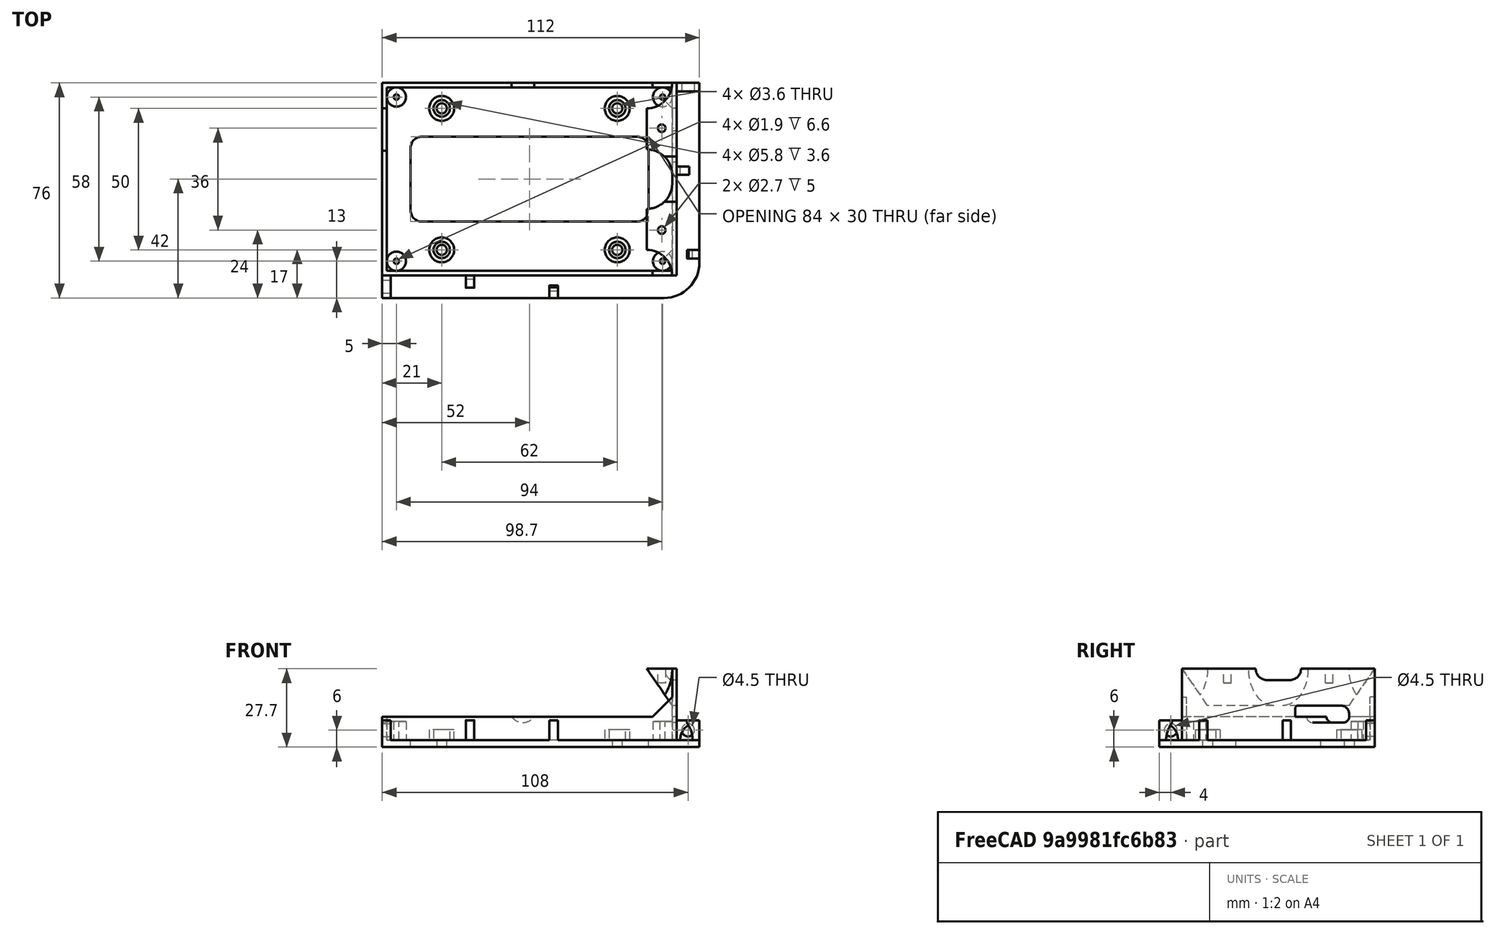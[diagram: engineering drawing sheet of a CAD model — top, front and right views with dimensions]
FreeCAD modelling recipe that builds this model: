
FCSTD DOCUMENT  (FreeCAD 1.0R39319 (Git))
Label: NanoPC-Rail
License: All rights reserved
LicenseURL: https://en.wikipedia.org/wiki/All_rights_reserved
objects: Sketcher::SketchObject×22, PartDesign::Pocket×13, PartDesign::Pad×9, App::VarSet×1, PartDesign::Body×1
note: 111 computed .brp shape members not serialized (recipe doc carries the construction recipe); baked Part::Feature solids carry a one-line shape summary decoded from their .brp

FEATURE [App::VarSet] VarSet
  BlackSelfTappingDiameter = 2.7
  Border = 8.2
  DX = 104
  DY = 68
  HoleDX = 94
  HoleDY = 58
  M3HeadDiameter = 5.8
  M3PassThroughDiameter = 3.6
  MiniBlackSelfTappingDiameter = 1.9
  PcbDX = 100.8
  PcbDY = 64.8
  PoleDiameter = 6.8
  PoleHeight = 6.6
  RailScrewDistance = 62
  Thickness = 2.5
  TopPcbWallHeight = 17
  WallThickness = 1.6
  expr: DX = PcbDX + 2 * WallThickness
  expr: DY = PcbDY + 2 * WallThickness
FEATURE [Sketcher::SketchObject] Sketch
  ArcFitTolerance = 1e-06
  AttachmentSupport = -> [XY_Plane]
  FullyConstrained = true
  MakeInternals = false
  MapMode = 5
  expr: Constraints[10] = VarSet.DY
  expr: Constraints[56] = VarSet.RailScrewDistance
  expr: Constraints[62] = VarSet.M3PassThroughDiameter
  expr: Constraints[9] = VarSet.DX
  sketch-geometry (29):
    g0: LineSegment StartX=-52 StartY=34 StartZ=0 EndX=-52 EndY=-34 EndZ=0
    g1: LineSegment [constr] StartX=-52 StartY=-34 StartZ=0 EndX=52 EndY=-34 EndZ=0
    g2: LineSegment [constr] StartX=52 StartY=-34 StartZ=0 EndX=52 EndY=34 EndZ=0
    g3: LineSegment StartX=52 StartY=34 StartZ=0 EndX=-52 EndY=34 EndZ=0
    g4: LineSegment StartX=-52 StartY=-34 StartZ=0 EndX=-52 EndY=-42 EndZ=0
    g5: LineSegment StartX=-52 StartY=-42 StartZ=0 EndX=47.5 EndY=-42 EndZ=0
    g6: LineSegment StartX=52 StartY=34 StartZ=0 EndX=60 EndY=34 EndZ=0
    g7: LineSegment StartX=60 StartY=34 StartZ=0 EndX=60 EndY=-29.5 EndZ=0
    g8: LineSegment StartX=-42 StartY=11 StartZ=0 EndX=-42 EndY=-11 EndZ=0
    g9: LineSegment StartX=-38 StartY=-15 StartZ=0 EndX=38 EndY=-15 EndZ=0
    g10: LineSegment StartX=42 StartY=-11 StartZ=0 EndX=42 EndY=11 EndZ=0
    g11: LineSegment StartX=38 StartY=15 StartZ=0 EndX=-38 EndY=15 EndZ=0
    g12: ArcOfCircle CenterX=-38 CenterY=11 CenterZ=0 NormalX=0 NormalY=0 NormalZ=1 AngleXU=0 Radius=4 StartAngle=1.5708 EndAngle=3.14159
    g13: ArcOfCircle CenterX=-38 CenterY=-11 CenterZ=0 NormalX=0 NormalY=0 NormalZ=1 AngleXU=0 Radius=4 StartAngle=3.14159 EndAngle=4.71239
    g14: ArcOfCircle CenterX=38 CenterY=-11 CenterZ=0 NormalX=0 NormalY=0 NormalZ=1 AngleXU=0 Radius=4 StartAngle=4.71239 EndAngle=6.28319
    g15: ArcOfCircle CenterX=38 CenterY=11 CenterZ=0 NormalX=0 NormalY=0 NormalZ=1 AngleXU=0 Radius=4 StartAngle=0 EndAngle=1.5708
    g16: GeomPoint [constr] X=-42 Y=15 Z=0
    g17: GeomPoint [constr] X=42 Y=-15 Z=0
    g18: LineSegment [constr] StartX=-42 StartY=11 StartZ=0 EndX=-52 EndY=11 EndZ=0
    g19: LineSegment [constr] StartX=-38 StartY=15 StartZ=0 EndX=-38 EndY=34 EndZ=0
    g20: ArcOfCircle CenterX=47.5 CenterY=-29.5 CenterZ=0 NormalX=0 NormalY=0 NormalZ=1 AngleXU=0 Radius=12.5 StartAngle=4.71239 EndAngle=6.28319
    g21: Circle CenterX=-31 CenterY=25 CenterZ=0 NormalX=0 NormalY=0 NormalZ=1 AngleXU=0 Radius=1.8
    g22: Circle CenterX=31 CenterY=25 CenterZ=0 NormalX=0 NormalY=0 NormalZ=1 AngleXU=0 Radius=1.8
    g23: LineSegment [constr] StartX=-31 StartY=25 StartZ=0 EndX=31 EndY=25 EndZ=0
    g24: LineSegment [constr] StartX=-31 StartY=25 StartZ=0 EndX=-31 EndY=34 EndZ=0
    g25: Circle CenterX=-31 CenterY=-25 CenterZ=0 NormalX=0 NormalY=0 NormalZ=1 AngleXU=0 Radius=1.8
    g26: Circle CenterX=31 CenterY=-25 CenterZ=0 NormalX=0 NormalY=0 NormalZ=1 AngleXU=0 Radius=1.8
    g27: LineSegment [constr] StartX=-31 StartY=-25 StartZ=0 EndX=31 EndY=-25 EndZ=0
    g28: LineSegment [constr] StartX=-31 StartY=-25 StartZ=0 EndX=-31 EndY=-34 EndZ=0
  constraints (73):
    c: Coincident(g0,g1)
    c: Coincident(g1,g2)
    c: Coincident(g2,g3)
    c: Coincident(g3,g0)
    c: Vertical(g0)
    c: Vertical(g2)
    c: Horizontal(g1)
    c: Horizontal(g3)
    c: Symmetric(g1,g0,g-1)
    c: Distance(g3) = 104
    c: Distance(g2) = 68
    c: Coincident(g4,g0)
    c: Vertical(g4)
    c: Coincident(g5,g4)
    c: Horizontal(g5)
    c: Coincident(g6,g2)
    c: Horizontal(g6)
    c: Coincident(g7,g6)
    c: Vertical(g7)
    c: Equal(g6,g4)
    c: Distance(g4) = 8
    c: Tangent(g8,g12) = -1.5708
    c: Tangent(g8,g13) = -1.5708
    c: Tangent(g9,g13) = -1.5708
    c: Tangent(g9,g14) = -1.5708
    c: Tangent(g10,g14) = -1.5708
    c: Tangent(g10,g15) = -1.5708
    c: Tangent(g11,g15) = -1.5708
    c: Tangent(g11,g12) = -1.5708
    c: Vertical(g8)
    c: Vertical(g10)
    c: Horizontal(g9)
    c: Horizontal(g11)
    c: Equal(g12,g13)
    c: Equal(g13,g14)
    c: Equal(g14,g15)
    c: PointOnObject(g16,g8)
    c: PointOnObject(g16,g11)
    c: PointOnObject(g17,g9)
    c: PointOnObject(g17,g10)
    c: Diameter(g15) = 8
    c: Symmetric(g16,g17,g-1)
    c: Coincident(g18,g8)
    c: PointOnObject(g18,g0)
    c: Horizontal(g18)
    c: Distance(g18) = 10
    c: Coincident(g19,g11)
    c: PointOnObject(g19,g3)
    c: Vertical(g19)
    c: Distance(g19) = 19
    c: Diameter(g20) = 25
    c: Tangent(g7,g20) = 1.5708
    c: Tangent(g5,g20) = -1.5708
    c: Symmetric(g21,g22,g-2)
    c: Coincident(g23,g21)
    c: Coincident(g23,g22)
    c: Distance(g23) = 62
    c: Coincident(g24,g21)
    c: PointOnObject(g24,g3)
    c: Vertical(g24)
    c: Distance(g24) = 9
    c: Equal(g22,g21)
    c: Diameter(g22) = 3.6
    c: Symmetric(g25,g26,g-2)
    c: Coincident(g27,g25)
    c: Coincident(g27,g26)
    c: Equal(g27,g23)
    c: Coincident(g28,g25)
    c: PointOnObject(g28,g1)
    c: Vertical(g28)
    c: Equal(g28,g24)
    c: Equal(g22,g26)
    c: Equal(g26,g25)
FEATURE [PartDesign::Pad] Pad  label="Base Structure"
  Direction = (0,0,1)
  Length = 2.5
  Length2 = 10
  Profile = -> Sketch
  ReferenceAxis = -> Sketch [N_Axis]
  Refine = true
  Suppressed = false
  Type = 0
  expr: Length = VarSet.Thickness
FEATURE [Sketcher::SketchObject] Sketch002
  ArcFitTolerance = 1e-06
  FullyConstrained = true
  MakeInternals = false
  MapMode = 5
  Placement = pos=(0,0,2.5) rot=(0,0,1;0rad)
  expr: Constraints[10] = VarSet.PcbDX
  expr: Constraints[17] = VarSet.DX
  expr: Constraints[20] = VarSet.DY
  expr: Constraints[9] = VarSet.PcbDY
  sketch-geometry (8):
    g0: LineSegment StartX=-50.4 StartY=32.4 StartZ=0 EndX=-50.4 EndY=-32.4 EndZ=0
    g1: LineSegment StartX=-50.4 StartY=-32.4 StartZ=0 EndX=50.4 EndY=-32.4 EndZ=0
    g2: LineSegment StartX=50.4 StartY=-32.4 StartZ=0 EndX=50.4 EndY=32.4 EndZ=0
    g3: LineSegment StartX=50.4 StartY=32.4 StartZ=0 EndX=-50.4 EndY=32.4 EndZ=0
    g4: LineSegment StartX=-52 StartY=34 StartZ=0 EndX=-52 EndY=-34 EndZ=0
    g5: LineSegment StartX=-52 StartY=-34 StartZ=0 EndX=52 EndY=-34 EndZ=0
    g6: LineSegment StartX=52 StartY=-34 StartZ=0 EndX=52 EndY=34 EndZ=0
    g7: LineSegment StartX=52 StartY=34 StartZ=0 EndX=-52 EndY=34 EndZ=0
  constraints (21):
    c: Coincident(g0,g1)
    c: Coincident(g1,g2)
    c: Coincident(g2,g3)
    c: Coincident(g3,g0)
    c: Vertical(g0)
    c: Vertical(g2)
    c: Horizontal(g1)
    c: Horizontal(g3)
    c: Symmetric(g1,g0,g-1)
    c: Distance(g2) = 64.8
    c: Distance(g3) = 100.8
    c: Coincident(g4,g5)
    c: Coincident(g5,g6)
    c: Coincident(g6,g7)
    c: Coincident(g7,g4)
    c: Horizontal(g5)
    c: Symmetric(g6,g4,g-2)
    c: Distance(g7) = 104
    c: Equal(g5,g7)
    c: Symmetric(g5,g6,g-1)
    c: Distance(g6) = 68
FEATURE [PartDesign::Pad] Pad001  label="Border"
  BaseFeature = -> Pad
  Direction = (0,0,1)
  Length = 8.2
  Length2 = 10
  Profile = -> Sketch002
  ReferenceAxis = -> Sketch002 [N_Axis]
  Refine = true
  Suppressed = false
  Type = 0
  expr: Length = VarSet.Border
FEATURE [Sketcher::SketchObject] Sketch003
  ArcFitTolerance = 1e-06
  AttachmentSupport = -> [Pad001]
  FullyConstrained = true
  MakeInternals = false
  MapMode = 5
  Placement = pos=(0,0,2.5) rot=(0,0,1;0rad)
  expr: Constraints[12] = VarSet.PoleDiameter
  expr: Constraints[20] = VarSet.MiniBlackSelfTappingDiameter
  expr: Constraints[5] = VarSet.HoleDX
  expr: Constraints[6] = VarSet.HoleDY
  sketch-geometry (10):
    g0: Circle CenterX=-47 CenterY=29 CenterZ=0 NormalX=0 NormalY=0 NormalZ=1 AngleXU=0 Radius=3.4
    g1: Circle CenterX=47 CenterY=29 CenterZ=0 NormalX=0 NormalY=0 NormalZ=1 AngleXU=0 Radius=3.4
    g2: Circle CenterX=47 CenterY=-29 CenterZ=0 NormalX=0 NormalY=0 NormalZ=1 AngleXU=0 Radius=3.4
    g3: Circle CenterX=-47 CenterY=-29 CenterZ=0 NormalX=0 NormalY=0 NormalZ=1 AngleXU=0 Radius=3.4
    g4: LineSegment [constr] StartX=-47 StartY=29 StartZ=0 EndX=47 EndY=29 EndZ=0
    g5: LineSegment [constr] StartX=47 StartY=29 StartZ=0 EndX=47 EndY=-29 EndZ=0
    g6: Circle CenterX=-47 CenterY=29 CenterZ=0 NormalX=0 NormalY=0 NormalZ=1 AngleXU=0 Radius=0.95
    g7: Circle CenterX=47 CenterY=29 CenterZ=0 NormalX=0 NormalY=0 NormalZ=1 AngleXU=0 Radius=0.95
    g8: Circle CenterX=47 CenterY=-29 CenterZ=0 NormalX=0 NormalY=0 NormalZ=1 AngleXU=0 Radius=0.95
    g9: Circle CenterX=-47 CenterY=-29 CenterZ=0 NormalX=0 NormalY=0 NormalZ=1 AngleXU=0 Radius=0.95
  constraints (21):
    c: Coincident(g4,g0)
    c: Coincident(g5,g1)
    c: Coincident(g5,g2)
    c: Coincident(g4,g1)
    c: Symmetric(g1,g0,g-2)
    c: Distance(g4) = 94
    c: Distance(g5) = 58
    c: Symmetric(g2,g1,g-1)
    c: Symmetric(g3,g2,g-2)
    c: Equal(g1,g2)
    c: Equal(g2,g3)
    c: Equal(g3,g0)
    c: Diameter(g3) = 6.8
    c: Coincident(g6,g0)
    c: Coincident(g7,g1)
    c: Coincident(g8,g2)
    c: Coincident(g9,g3)
    c: Equal(g9,g6)
    c: Equal(g6,g8)
    c: Equal(g8,g7)
    c: Diameter(g6) = 1.9
FEATURE [PartDesign::Pad] Pad002  label="Screw Poles"
  BaseFeature = -> Pad001
  Direction = (0,0,1)
  Length = 6.6
  Length2 = 10
  Profile = -> Sketch003
  ReferenceAxis = -> Sketch003 [N_Axis]
  Refine = true
  Suppressed = false
  Type = 0
  expr: Length = VarSet.PoleHeight
FEATURE [Sketcher::SketchObject] Sketch004
  ArcFitTolerance = 1e-06
  AttachmentSupport = -> [Pad002]
  ExternalGeometry = -> [Pad002]
  FullyConstrained = true
  MakeInternals = false
  MapMode = 5
  Placement = pos=(0,0,2.5) rot=(0,0,1;0rad)
  sketch-geometry (36):
    g0: LineSegment [constr] StartX=-52 StartY=-34 StartZ=0 EndX=-52 EndY=-42 EndZ=0
    g1: LineSegment [constr] StartX=-52 StartY=-42 StartZ=0 EndX=10 EndY=-42 EndZ=0
    g2: LineSegment [constr] StartX=10 StartY=-42 StartZ=0 EndX=10 EndY=-34 EndZ=0
    g3: LineSegment [constr] StartX=10 StartY=-34 StartZ=0 EndX=-52 EndY=-34 EndZ=0
    g4: LineSegment [constr] StartX=52 StartY=34 StartZ=0 EndX=52 EndY=-28 EndZ=0
    g5: LineSegment [constr] StartX=52 StartY=-28 StartZ=0 EndX=60 EndY=-28 EndZ=0
    g6: LineSegment [constr] StartX=60 StartY=-28 StartZ=0 EndX=60 EndY=34 EndZ=0
    g7: LineSegment [constr] StartX=60 StartY=34 StartZ=0 EndX=52 EndY=34 EndZ=0
    g8: LineSegment StartX=-52 StartY=-34 StartZ=0 EndX=-52 EndY=-42 EndZ=0
    g9: LineSegment StartX=-52 StartY=-42 StartZ=0 EndX=-49 EndY=-42 EndZ=0
    g10: LineSegment StartX=-49 StartY=-42 StartZ=0 EndX=-49 EndY=-34 EndZ=0
    g11: LineSegment StartX=-49 StartY=-34 StartZ=0 EndX=-52 EndY=-34 EndZ=0
    g12: LineSegment StartX=-22.5 StartY=-34 StartZ=0 EndX=-22.5 EndY=-38.4 EndZ=0
    g13: LineSegment StartX=-22.5 StartY=-38.4 StartZ=0 EndX=-19.5 EndY=-38.4 EndZ=0
    g14: LineSegment StartX=-19.5 StartY=-38.4 StartZ=0 EndX=-19.5 EndY=-34 EndZ=0
    g15: LineSegment StartX=-19.5 StartY=-34 StartZ=0 EndX=-22.5 EndY=-34 EndZ=0
    g16: LineSegment StartX=10 StartY=-42 StartZ=0 EndX=10 EndY=-37.6 EndZ=0
    g17: LineSegment StartX=10 StartY=-37.6 StartZ=0 EndX=7 EndY=-37.6 EndZ=0
    g18: LineSegment StartX=7 StartY=-37.6 StartZ=0 EndX=7 EndY=-42 EndZ=0
    g19: LineSegment StartX=7 StartY=-42 StartZ=0 EndX=10 EndY=-42 EndZ=0
    g20: LineSegment StartX=52 StartY=34 StartZ=0 EndX=52 EndY=31 EndZ=0
    g21: LineSegment StartX=52 StartY=31 StartZ=0 EndX=60 EndY=31 EndZ=0
    g22: LineSegment StartX=60 StartY=31 StartZ=0 EndX=60 EndY=34 EndZ=0
    g23: LineSegment StartX=60 StartY=34 StartZ=0 EndX=52 EndY=34 EndZ=0
    g24: LineSegment StartX=52 StartY=4.5 StartZ=0 EndX=52 EndY=1.5 EndZ=0
    g25: LineSegment StartX=52 StartY=1.5 StartZ=0 EndX=56.4 EndY=1.5 EndZ=0
    g26: LineSegment StartX=56.4 StartY=1.5 StartZ=0 EndX=56.4 EndY=4.5 EndZ=0
    g27: LineSegment StartX=56.4 StartY=4.5 StartZ=0 EndX=52 EndY=4.5 EndZ=0
    g28: LineSegment StartX=60 StartY=-28 StartZ=0 EndX=60 EndY=-25 EndZ=0
    g29: LineSegment StartX=60 StartY=-25 StartZ=0 EndX=55.6 EndY=-25 EndZ=0
    g30: LineSegment StartX=55.6 StartY=-25 StartZ=0 EndX=55.6 EndY=-28 EndZ=0
    g31: LineSegment StartX=55.6 StartY=-28 StartZ=0 EndX=60 EndY=-28 EndZ=0
    g32: LineSegment [constr] StartX=-52 StartY=-42 StartZ=0 EndX=-22.5 EndY=-38.4 EndZ=0
    g33: LineSegment [constr] StartX=10 StartY=-42 StartZ=0 EndX=-19.5 EndY=-38.4 EndZ=0
    g34: LineSegment [constr] StartX=56.4 StartY=1.5 StartZ=0 EndX=60 EndY=-28 EndZ=0
    g35: LineSegment [constr] StartX=56.4 StartY=4.5 StartZ=0 EndX=60 EndY=34 EndZ=0
  constraints (98):
    c: Coincident(g0,g1)
    c: Coincident(g1,g2)
    c: Coincident(g2,g3)
    c: Coincident(g3,g0)
    c: Vertical(g0)
    c: Vertical(g2)
    c: Horizontal(g1)
    c: Horizontal(g3)
    c: Coincident(g4,g5)
    c: Coincident(g5,g6)
    c: Coincident(g6,g7)
    c: Coincident(g7,g4)
    c: Vertical(g4)
    c: Vertical(g6)
    c: Horizontal(g5)
    c: Horizontal(g7)
    c: Equal(g5,g2)
    c: Distance(g7) = 8
    c: Coincident(g6,g-4)
    c: Coincident(g0,g-3)
    c: Distance(g1) = 62
    c: Equal(g1,g6)
    c: Coincident(g8,g9)
    c: Coincident(g9,g10)
    c: Coincident(g10,g11)
    c: Coincident(g11,g8)
    c: Vertical(g8)
    c: Vertical(g10)
    c: Horizontal(g9)
    c: Horizontal(g11)
    c: Coincident(g8,g0)
    c: PointOnObject(g9,g1)
    c: Distance(g9) = 3
    c: Coincident(g12,g13)
    c: Coincident(g13,g14)
    c: Coincident(g14,g15)
    c: Coincident(g15,g12)
    c: Vertical(g12)
    c: Vertical(g14)
    c: Horizontal(g13)
    c: Horizontal(g15)
    c: Equal(g9,g13)
    c: Coincident(g16,g17)
    c: Coincident(g17,g18)
    c: Coincident(g18,g19)
    c: Coincident(g19,g16)
    c: Vertical(g16)
    c: Vertical(g18)
    c: Horizontal(g17)
    c: Horizontal(g19)
    c: Coincident(g16,g1)
    c: Equal(g19,g13)
    c: Coincident(g20,g21)
    c: Coincident(g21,g22)
    c: Coincident(g22,g23)
    c: Coincident(g23,g20)
    c: Vertical(g20)
    c: Vertical(g22)
    c: Horizontal(g21)
    c: Horizontal(g23)
    c: Coincident(g20,g4)
    c: PointOnObject(g21,g6)
    c: Equal(g19,g22)
    c: Coincident(g24,g25)
    c: Coincident(g25,g26)
    c: Coincident(g26,g27)
    c: Coincident(g27,g24)
    c: Vertical(g24)
    c: Vertical(g26)
    c: Horizontal(g25)
    c: Horizontal(g27)
    c: Coincident(g28,g29)
    c: Coincident(g29,g30)
    c: Coincident(g30,g31)
    c: Coincident(g31,g28)
    c: Vertical(g28)
    c: Vertical(g30)
    c: Horizontal(g29)
    c: Horizontal(g31)
    c: Coincident(g28,g5)
    c: Equal(g28,g26)
    c: Equal(g26,g19)
    c: Distance(g12) = 4.4
    c: Distance(g27) = 4.4
    c: PointOnObject(g14,g3)
    c: Equal(g14,g18)
    c: Coincident(g32,g0)
    c: Coincident(g32,g12)
    c: Coincident(g33,g1)
    c: Coincident(g33,g13)
    c: Equal(g33,g32)
    c: PointOnObject(g24,g4)
    c: Equal(g25,g29)
    c: Coincident(g34,g25)
    c: Coincident(g34,g5)
    c: Coincident(g35,g26)
    c: Coincident(g35,g6)
    c: Equal(g34,g35)
FEATURE [Sketcher::SketchObject] Sketch015
  ArcFitTolerance = 1e-06
  AttachmentSupport = -> [Pad002]
  ExternalGeometry = -> [Pad002]
  FullyConstrained = true
  MakeInternals = false
  MapMode = 5
  Placement = pos=(0,0,2.5) rot=(0,0,1;0rad)
  expr: Constraints[15] = VarSet.M3HeadDiameter + 3 mm
  expr: Constraints[7] = VarSet.M3HeadDiameter
  sketch-geometry (8):
    g0: Circle CenterX=-31 CenterY=25 CenterZ=0 NormalX=0 NormalY=0 NormalZ=1 AngleXU=0 Radius=2.9
    g1: Circle CenterX=31 CenterY=25 CenterZ=0 NormalX=0 NormalY=0 NormalZ=1 AngleXU=0 Radius=2.9
    g2: Circle CenterX=31 CenterY=-25 CenterZ=0 NormalX=0 NormalY=0 NormalZ=1 AngleXU=0 Radius=2.9
    g3: Circle CenterX=-31 CenterY=-25 CenterZ=0 NormalX=0 NormalY=0 NormalZ=1 AngleXU=0 Radius=2.9
    g4: Circle CenterX=31 CenterY=25 CenterZ=0 NormalX=0 NormalY=0 NormalZ=1 AngleXU=0 Radius=4.4
    g5: Circle CenterX=31 CenterY=-25 CenterZ=0 NormalX=0 NormalY=0 NormalZ=1 AngleXU=0 Radius=4.4
    g6: Circle CenterX=-31 CenterY=-25 CenterZ=0 NormalX=0 NormalY=0 NormalZ=1 AngleXU=0 Radius=4.4
    g7: Circle CenterX=-31 CenterY=25 CenterZ=0 NormalX=0 NormalY=0 NormalZ=1 AngleXU=0 Radius=4.4
  constraints (16):
    c: Coincident(g0,g-3)
    c: Coincident(g1,g-4)
    c: Coincident(g2,g-5)
    c: Coincident(g3,g-6)
    c: Equal(g0,g1)
    c: Equal(g1,g2)
    c: Equal(g2,g3)
    c: Diameter(g1) = 5.8
    c: Coincident(g4,g1)
    c: Coincident(g5,g2)
    c: Coincident(g6,g3)
    c: Coincident(g7,g0)
    c: Equal(g6,g7)
    c: Equal(g7,g4)
    c: Equal(g4,g5)
    c: Diameter(g4) = 8.8
FEATURE [PartDesign::Pad] Pad004  label="Rail Clamp Screws"
  BaseFeature = -> Pad002
  Direction = (0,0,1)
  Length = 3.6
  Length2 = 10
  Profile = -> Sketch015
  ReferenceAxis = -> Sketch015 [N_Axis]
  Refine = true
  Suppressed = false
  Type = 0
FEATURE [PartDesign::Pad] Pad003  label="Antenna Holders"
  BaseFeature = -> Pad004
  Direction = (0,0,1)
  Length = 7
  Length2 = 10
  Profile = -> Sketch004
  ReferenceAxis = -> Sketch004 [N_Axis]
  Refine = true
  Suppressed = false
  Type = 0
FEATURE [Sketcher::SketchObject] Sketch005
  ArcFitTolerance = 1e-06
  AttachmentSupport = -> [Pad003]
  ExternalGeometry = -> [Pad003]
  FullyConstrained = true
  MakeInternals = false
  MapMode = 5
  Placement = pos=(-49,0,0) rot=(0.57735,0.57735,0.57735;2.0944rad)
  sketch-geometry (1):
    g0: Circle CenterX=-38 CenterY=6 CenterZ=0 NormalX=0 NormalY=0 NormalZ=1 AngleXU=0 Radius=2.25
  constraints (2):
    c: Symmetric(g-4,g-3,g0)
    c: Diameter(g0) = 4.5
FEATURE [PartDesign::Pocket] Pocket001  label="Hole 1"
  BaseFeature = -> Pad003
  Direction = (-1,0,0)
  Length = 5
  Length2 = 2
  Profile = -> Sketch005
  ReferenceAxis = -> Sketch005 [N_Axis]
  Refine = true
  Suppressed = false
  Type = 0
FEATURE [Sketcher::SketchObject] Sketch006
  ArcFitTolerance = 1e-06
  AttachmentSupport = -> [Pocket001]
  ExternalGeometry = -> [Pocket001]
  FullyConstrained = true
  MakeInternals = false
  MapMode = 5
  Placement = pos=(0,31,0) rot=(1,0,0;1.5708rad)
  sketch-geometry (1):
    g0: Circle CenterX=56 CenterY=6 CenterZ=0 NormalX=0 NormalY=0 NormalZ=1 AngleXU=0 Radius=2.25
  constraints (2):
    c: Diameter(g0) = 4.5
    c: Symmetric(g-4,g-3,g0)
FEATURE [PartDesign::Pocket] Pocket002  label="Hole 2"
  BaseFeature = -> Pocket001
  Direction = (0,1,-2e-16)
  Length = 5
  Length2 = 5
  Profile = -> Sketch006
  ReferenceAxis = -> Sketch006 [N_Axis]
  Refine = true
  Suppressed = false
  Type = 0
FEATURE [Sketcher::SketchObject] Sketch007
  ArcFitTolerance = 1e-06
  AttachmentSupport = -> [Pocket002]
  ExternalGeometry = -> [Pocket002]
  FullyConstrained = true
  MakeInternals = false
  MapMode = 5
  Placement = pos=(0,1.5,0) rot=(1,0,0;1.5708rad)
  sketch-geometry (5):
    g0: LineSegment StartX=56.4 StartY=9.5 StartZ=0 EndX=55.4 EndY=9.5 EndZ=0
    g1: LineSegment StartX=56.4 StartY=2.5 StartZ=0 EndX=53.2 EndY=2.5 EndZ=0
    g2: ArcOfCircle CenterX=55.4 CenterY=8.5 CenterZ=0 NormalX=0 NormalY=0 NormalZ=1 AngleXU=0 Radius=1 StartAngle=5.30327 EndAngle=7.85398
    g3: LineSegment StartX=56.4 StartY=9.5 StartZ=0 EndX=56.4 EndY=2.5 EndZ=0
    g4: ArcOfCircle CenterX=59.425 CenterY=2.5 CenterZ=0 NormalX=0 NormalY=0 NormalZ=1 AngleXU=0 Radius=6.225 StartAngle=2.16168 EndAngle=3.14159
  constraints (14):
    c: Coincident(g0,g-3)
    c: Horizontal(g0)
    c: Coincident(g1,g-3)
    c: Horizontal(g1)
    c: Distance(g0) = 1
    c: Distance(g1) = 3.2
    c: Coincident(g2,g0)
    c: Diameter(g2) = 2
    c: Tangent(g2,g-3)
    c: Coincident(g3,g0)
    c: Coincident(g3,g1)
    c: Coincident(g4,g1)
    c: Perpendicular(g4,g1)
    c: Tangent(g4,g2) = 1.5708
FEATURE [PartDesign::Pocket] Pocket003  label="Hook 1"
  BaseFeature = -> Pocket002
  Direction = (0,1,-2e-16)
  Length = 5
  Length2 = 5
  Profile = -> Sketch007
  ReferenceAxis = -> Sketch007 [N_Axis]
  Refine = true
  Suppressed = false
  Type = 0
FEATURE [Sketcher::SketchObject] Sketch008
  ArcFitTolerance = 1e-06
  AttachmentSupport = -> [Pocket003]
  ExternalGeometry = -> [Pocket003]
  FullyConstrained = true
  MakeInternals = false
  MapMode = 5
  Placement = pos=(0,-28,0) rot=(1,0,0;1.5708rad)
  sketch-geometry (5):
    g0: LineSegment StartX=55.6 StartY=9.5 StartZ=0 EndX=56.6 EndY=9.5 EndZ=0
    g1: LineSegment StartX=55.6 StartY=2.5 StartZ=0 EndX=57.6 EndY=2.5 EndZ=0
    g2: ArcOfCircle CenterX=56.4 CenterY=8.7254 CenterZ=0 NormalX=0 NormalY=0 NormalZ=1 AngleXU=0 Radius=0.8 StartAngle=1.31812 EndAngle=3.76329
    g3: ArcOfCircle CenterX=47.7111 CenterY=2.5 CenterZ=0 NormalX=0 NormalY=0 NormalZ=1 AngleXU=0 Radius=9.88891 StartAngle=-9e-16 EndAngle=0.621699
    g4: LineSegment StartX=55.6 StartY=9.5 StartZ=0 EndX=55.6 EndY=2.5 EndZ=0
  constraints (14):
    c: Coincident(g0,g-3)
    c: Horizontal(g0)
    c: Coincident(g1,g-3)
    c: Horizontal(g1)
    c: Distance(g0) = 1
    c: Distance(g1) = 2
    c: Coincident(g2,g0)
    c: Diameter(g2) = 1.6
    c: Tangent(g-3,g2)
    c: Coincident(g3,g1)
    c: Perpendicular(g3,g1)
    c: Tangent(g3,g2) = 1.5708
    c: Coincident(g4,g0)
    c: Coincident(g4,g1)
FEATURE [PartDesign::Pocket] Pocket004  label="Hook 2"
  BaseFeature = -> Pocket003
  Direction = (0,1,-2e-16)
  Length = 5
  Length2 = 5
  Profile = -> Sketch008
  ReferenceAxis = -> Sketch008 [N_Axis]
  Refine = true
  Suppressed = false
  Type = 0
FEATURE [Sketcher::SketchObject] Sketch009
  ArcFitTolerance = 1e-06
  AttachmentSupport = -> [Pocket004]
  ExternalGeometry = -> [Pocket004]
  FullyConstrained = true
  MakeInternals = false
  MapMode = 5
  Placement = pos=(10,0,0) rot=(0.57735,0.57735,0.57735;2.0944rad)
  sketch-geometry (5):
    g0: LineSegment StartX=-37.6 StartY=9.5 StartZ=0 EndX=-38.6 EndY=9.5 EndZ=0
    g1: LineSegment StartX=-37.6 StartY=2.5 StartZ=0 EndX=-39.6 EndY=2.5 EndZ=0
    g2: ArcOfCircle CenterX=-38.4 CenterY=8.7254 CenterZ=0 NormalX=0 NormalY=0 NormalZ=1 AngleXU=0 Radius=0.8 StartAngle=5.66149 EndAngle=8.10666
    g3: ArcOfCircle CenterX=-29.7111 CenterY=2.5 CenterZ=0 NormalX=0 NormalY=0 NormalZ=1 AngleXU=0 Radius=9.88891 StartAngle=2.51989 EndAngle=3.14159
    g4: LineSegment StartX=-37.6 StartY=9.5 StartZ=0 EndX=-37.6 EndY=2.5 EndZ=0
  constraints (14):
    c: Coincident(g0,g-3)
    c: Horizontal(g0)
    c: Coincident(g1,g-3)
    c: Horizontal(g1)
    c: Distance(g1) = 2
    c: Distance(g0) = 1
    c: Coincident(g2,g0)
    c: Diameter(g2) = 1.6
    c: Tangent(g2,g-3)
    c: Coincident(g3,g1)
    c: Perpendicular(g3,g1)
    c: Tangent(g3,g2) = 1.5708
    c: Coincident(g4,g0)
    c: Coincident(g4,g1)
FEATURE [PartDesign::Pocket] Pocket005  label="Hook 3"
  BaseFeature = -> Pocket004
  Direction = (-1,0,0)
  Length = 5
  Length2 = 5
  Profile = -> Sketch009
  ReferenceAxis = -> Sketch009 [N_Axis]
  Refine = true
  Suppressed = false
  Type = 0
FEATURE [Sketcher::SketchObject] Sketch010
  ArcFitTolerance = 1e-06
  AttachmentSupport = -> [Pocket005]
  ExternalGeometry = -> [Pocket005]
  FullyConstrained = true
  MakeInternals = false
  MapMode = 5
  Placement = pos=(-19.5,0,0) rot=(0.57735,0.57735,0.57735;2.0944rad)
  sketch-geometry (5):
    g0: LineSegment StartX=-38.4 StartY=9.5 StartZ=0 EndX=-37.4 EndY=9.5 EndZ=0
    g1: LineSegment StartX=-38.4 StartY=2.5 StartZ=0 EndX=-35.4 EndY=2.5 EndZ=0
    g2: ArcOfCircle CenterX=-37.4 CenterY=8.5 CenterZ=0 NormalX=0 NormalY=0 NormalZ=1 AngleXU=0 Radius=1 StartAngle=1.5708 EndAngle=4.06889
    g3: ArcOfCircle CenterX=-41.9 CenterY=2.5 CenterZ=0 NormalX=0 NormalY=0 NormalZ=1 AngleXU=0 Radius=6.5 StartAngle=0 EndAngle=0.927295
    g4: LineSegment StartX=-38.4 StartY=9.5 StartZ=0 EndX=-38.4 EndY=2.5 EndZ=0
  constraints (14):
    c: Coincident(g0,g-3)
    c: Horizontal(g0)
    c: Coincident(g1,g-3)
    c: Horizontal(g1)
    c: Distance(g0) = 1
    c: Distance(g1) = 3
    c: Coincident(g2,g0)
    c: Diameter(g2) = 2
    c: Tangent(g2,g-3)
    c: Coincident(g3,g1)
    c: Perpendicular(g3,g1)
    c: Tangent(g3,g2) = 1.5708
    c: Coincident(g4,g0)
    c: Coincident(g4,g1)
FEATURE [PartDesign::Pocket] Pocket006  label="Hook 4"
  BaseFeature = -> Pocket005
  Direction = (-1,0,0)
  Length = 5
  Length2 = 5
  Profile = -> Sketch010
  ReferenceAxis = -> Sketch010 [N_Axis]
  Refine = true
  Suppressed = false
  Type = 0
FEATURE [Sketcher::SketchObject] Sketch012
  ArcFitTolerance = 1e-06
  AttachmentSupport = -> [Pocket006]
  FullyConstrained = true
  MakeInternals = false
  MapMode = 5
  Placement = pos=(0,34,0) rot=(0,0.707107,0.707107;3.14159rad)
  expr: Constraints[11] = VarSet.Border + VarSet.Thickness + 3 mm
  sketch-geometry (5):
    g0: Circle CenterX=2.3 CenterY=13.7 CenterZ=0 NormalX=0 NormalY=0 NormalZ=1 AngleXU=0 Radius=5
    g1: LineSegment [constr] StartX=0 StartY=0 StartZ=0 EndX=2.3 EndY=0 EndZ=0
    g2: LineSegment [constr] StartX=2.3 StartY=0 StartZ=0 EndX=2.3 EndY=13.7 EndZ=0
    g3: LineSegment [constr] StartX=2.3 StartY=13.7 StartZ=0 EndX=0 EndY=13.7 EndZ=0
    g4: LineSegment [constr] StartX=0 StartY=13.7 StartZ=0 EndX=0 EndY=0 EndZ=0
  constraints (13):
    c: Diameter(g0) = 10
    c: Coincident(g1,g2)
    c: Coincident(g2,g3)
    c: Coincident(g3,g4)
    c: Coincident(g4,g1)
    c: Horizontal(g1)
    c: Horizontal(g3)
    c: Vertical(g2)
    c: Vertical(g4)
    c: Coincident(g1,g-1)
    c: Distance(g1) = 2.3
    c: Distance(g4) = 13.7
    c: Coincident(g0,g2)
FEATURE [PartDesign::Pocket] Pocket008  label="Audio Jack"
  BaseFeature = -> Pocket006
  Direction = (0,-1,2e-16)
  Length = 5
  Length2 = 5
  Profile = -> Sketch012
  ReferenceAxis = -> Sketch012 [N_Axis]
  Refine = true
  Suppressed = false
  Type = 0
FEATURE [Sketcher::SketchObject] Sketch013
  ArcFitTolerance = 1e-06
  AttachmentSupport = -> [Pocket008]
  ExternalGeometry = -> [Pocket008]
  FullyConstrained = true
  MakeInternals = false
  MapMode = 5
  Placement = pos=(-52,0,2.91e-14) rot=(0.57735,-0.57735,-0.57735;2.0944rad)
  sketch-geometry (5):
    g0: LineSegment [constr] StartX=-34 StartY=10.7 StartZ=0 EndX=-25 EndY=10.7 EndZ=0
    g1: LineSegment StartX=-25 StartY=10.7 StartZ=0 EndX=-10 EndY=10.7 EndZ=0
    g2: ArcOfCircle CenterX=-23 CenterY=10.7 CenterZ=0 NormalX=0 NormalY=0 NormalZ=1 AngleXU=0 Radius=2 StartAngle=3.14159 EndAngle=4.71239
    g3: ArcOfCircle CenterX=-12 CenterY=10.7 CenterZ=0 NormalX=0 NormalY=0 NormalZ=1 AngleXU=0 Radius=2 StartAngle=4.71239 EndAngle=6.28319
    g4: LineSegment StartX=-23 StartY=8.7 StartZ=0 EndX=-12 EndY=8.7 EndZ=0
  constraints (14):
    c: Horizontal(g0)
    c: Distance(g0) = 9
    c: Coincident(g1,g0)
    c: Horizontal(g1)
    c: Distance(g1) = 15
    c: Coincident(g2,g0)
    c: Coincident(g3,g1)
    c: Perpendicular(g3,g1)
    c: Perpendicular(g2,g1)
    c: Horizontal(g4)
    c: Tangent(g4,g2) = -1.5708
    c: Tangent(g4,g3) = -1.5708
    c: Diameter(g2) = 4
    c: Coincident(g0,g-3)
FEATURE [PartDesign::Pocket] Pocket009  label="Buttons"
  BaseFeature = -> Pocket008
  Direction = (1,0,0)
  Length = 3
  Length2 = 5
  Profile = -> Sketch013
  ReferenceAxis = -> Sketch013 [N_Axis]
  Refine = true
  Suppressed = false
  Type = 0
FEATURE [Sketcher::SketchObject] Sketch014
  ArcFitTolerance = 1e-06
  AttachmentSupport = -> [Pocket009]
  ExternalGeometry = -> [Pocket009]
  FullyConstrained = true
  MakeInternals = false
  MapMode = 5
  Placement = pos=(52,0,0) rot=(0.57735,0.57735,0.57735;2.0944rad)
  sketch-geometry (5):
    g0: LineSegment [constr] StartX=34 StartY=10.7 StartZ=0 EndX=25 EndY=10.7 EndZ=0
    g1: LineSegment StartX=25 StartY=10.7 StartZ=0 EndX=17 EndY=10.7 EndZ=0
    g2: ArcOfCircle CenterX=19 CenterY=10.7 CenterZ=0 NormalX=0 NormalY=0 NormalZ=1 AngleXU=0 Radius=2 StartAngle=3.14159 EndAngle=4.71239
    g3: ArcOfCircle CenterX=23 CenterY=10.7 CenterZ=0 NormalX=0 NormalY=0 NormalZ=1 AngleXU=0 Radius=2 StartAngle=4.71239 EndAngle=6.28319
    g4: LineSegment StartX=19 StartY=8.7 StartZ=0 EndX=23 EndY=8.7 EndZ=0
  constraints (14):
    c: Coincident(g0,g-3)
    c: PointOnObject(g0,g-3)
    c: Distance(g0) = 9
    c: Coincident(g1,g0)
    c: PointOnObject(g1,g-3)
    c: Distance(g1) = 8
    c: PointOnObject(g2,g1)
    c: Coincident(g2,g1)
    c: PointOnObject(g3,g1)
    c: Coincident(g3,g0)
    c: Diameter(g2) = 4
    c: Horizontal(g4)
    c: Tangent(g4,g2) = -1.5708
    c: Tangent(g3,g4) = -1.5708
FEATURE [PartDesign::Pocket] Pocket010  label="Reset"
  BaseFeature = -> Pocket009
  Direction = (-1,0,0)
  Length = 3
  Length2 = 5
  Profile = -> Sketch014
  ReferenceAxis = -> Sketch014 [N_Axis]
  Refine = true
  Suppressed = false
  Type = 0
FEATURE [Sketcher::SketchObject] Sketch016
  ArcFitTolerance = 1e-06
  AttachmentSupport = -> [Pocket010]
  ExternalGeometry = -> [Pocket010]
  FullyConstrained = true
  MakeInternals = false
  MapMode = 5
  Placement = pos=(52,0,0) rot=(0.57735,0.57735,0.57735;2.0944rad)
  expr: Constraints[2] = VarSet.TopPcbWallHeight
  sketch-geometry (12):
    g0: LineSegment StartX=-34 StartY=10.7 StartZ=0 EndX=-34 EndY=27.7 EndZ=0
    g1: LineSegment StartX=-34 StartY=27.7 StartZ=0 EndX=34 EndY=27.7 EndZ=0
    g2: LineSegment StartX=34 StartY=10.7 StartZ=0 EndX=34 EndY=27.7 EndZ=0
    g3: LineSegment [constr] StartX=17 StartY=10.7 StartZ=0 EndX=6 EndY=10.7 EndZ=0
    g4: LineSegment StartX=-34 StartY=10.7 StartZ=0 EndX=6 EndY=10.7 EndZ=0
    g5: LineSegment StartX=6 StartY=10.7 StartZ=0 EndX=6 EndY=13.7 EndZ=0
    g6: LineSegment StartX=7 StartY=14.7 StartZ=0 EndX=22 EndY=14.7 EndZ=0
    g7: LineSegment [constr] StartX=17 StartY=10.7 StartZ=0 EndX=17 EndY=14.7 EndZ=0
    g8: ArcOfCircle CenterX=7 CenterY=13.7 CenterZ=0 NormalX=0 NormalY=0 NormalZ=1 AngleXU=0 Radius=1 StartAngle=1.5708 EndAngle=3.14159
    g9: LineSegment StartX=25 StartY=10.7 StartZ=0 EndX=25 EndY=11.7 EndZ=0
    g10: ArcOfCircle CenterX=22 CenterY=11.7 CenterZ=0 NormalX=0 NormalY=0 NormalZ=1 AngleXU=0 Radius=3 StartAngle=3e-16 EndAngle=1.5708
    g11: LineSegment StartX=25 StartY=10.7 StartZ=0 EndX=34 EndY=10.7 EndZ=0
  constraints (30):
    c: Coincident(g0,g-3)
    c: Vertical(g0)
    c: Distance(g0) = 17
    c: Coincident(g1,g0)
    c: Horizontal(g1)
    c: Coincident(g2,g-6)
    c: Vertical(g2)
    c: Coincident(g1,g2)
    c: Coincident(g3,g-4)
    c: Horizontal(g3)
    c: Distance(g3) = 11
    c: Coincident(g4,g0)
    c: Coincident(g4,g3)
    c: Coincident(g5,g3)
    c: Vertical(g5)
    c: Horizontal(g6)
    c: Coincident(g7,g3)
    c: PointOnObject(g7,g6)
    c: Vertical(g7)
    c: Distance(g7) = 4
    c: Diameter(g8) = 2
    c: Tangent(g8,g6) = 1.5708
    c: Tangent(g8,g5) = 1.5708
    c: Coincident(g9,g-5)
    c: Vertical(g9)
    c: Tangent(g10,g9) = -1.5708
    c: Tangent(g10,g6) = 1.5708
    c: Diameter(g10) = 6
    c: Coincident(g11,g9)
    c: Coincident(g11,g2)
FEATURE [PartDesign::Pad] Pad005  label="Wall to Floor"
  BaseFeature = -> Pocket010
  Direction = (1,0,0)
  Length = 1.6
  Length2 = 10
  Profile = -> Sketch016
  ReferenceAxis = -> Sketch016 [N_Axis]
  Refine = true
  Reversed = true
  Suppressed = false
  Type = 0
  expr: Length = VarSet.WallThickness
FEATURE [Sketcher::SketchObject] Sketch017
  ArcFitTolerance = 1e-06
  AttachmentSupport = -> [Pad005]
  ExternalGeometry = -> [Pad005]
  FullyConstrained = true
  MakeInternals = false
  MapMode = 5
  Placement = pos=(50.4,0,0) rot=(0.57735,-0.57735,-0.57735;2.0944rad)
  sketch-geometry (4):
    g0: LineSegment StartX=-34 StartY=27.7 StartZ=0 EndX=34 EndY=27.7 EndZ=0
    g1: LineSegment StartX=-25 StartY=14.7 StartZ=0 EndX=25 EndY=14.7 EndZ=0
    g2: LineSegment StartX=-25 StartY=14.7 StartZ=0 EndX=-34 EndY=27.7 EndZ=0
    g3: LineSegment StartX=25 StartY=14.7 StartZ=0 EndX=34 EndY=27.7 EndZ=0
  constraints (10):
    c: Horizontal(g1)
    c: Coincident(g2,g-3)
    c: Coincident(g3,g1)
    c: Coincident(g3,g-3)
    c: Equal(g3,g2)
    c: PointOnObject(g-4,g1)
    c: Coincident(g0,g3)
    c: Coincident(g0,g2)
    c: Coincident(g2,g1)
    c: Distance(g1) = 50
FEATURE [PartDesign::Pad] Pad006  label="Floor Block"
  BaseFeature = -> Pad005
  Direction = (-1,0,0)
  Length = 9
  Length2 = 10
  Profile = -> Sketch017
  ReferenceAxis = -> Sketch017 [N_Axis]
  Refine = true
  Suppressed = false
  Type = 0
FEATURE [Sketcher::SketchObject] Sketch018
  ArcFitTolerance = 1e-06
  AttachmentSupport = -> [Pad006]
  ExternalGeometry = -> [Pad006]
  FullyConstrained = true
  MakeInternals = false
  MapMode = 5
  Placement = pos=(0,34,0) rot=(0,0.707107,0.707107;3.14159rad)
  sketch-geometry (3):
    g0: LineSegment StartX=-50.4 StartY=14.7 StartZ=0 EndX=-41.4 EndY=27.7 EndZ=0
    g1: LineSegment StartX=-41.4 StartY=27.7 StartZ=0 EndX=-41.4 EndY=14.7 EndZ=0
    g2: LineSegment StartX=-41.4 StartY=14.7 StartZ=0 EndX=-50.4 EndY=14.7 EndZ=0
  constraints (6):
    c: Coincident(g0,g-4)
    c: Coincident(g0,g-3)
    c: Coincident(g1,g-3)
    c: Coincident(g1,g-4)
    c: Coincident(g2,g-4)
    c: Coincident(g2,g-4)
FEATURE [PartDesign::Pocket] Pocket  label="Floor Rise"
  BaseFeature = -> Pad006
  Direction = (0,-1,2e-16)
  Length = 5
  Length2 = 5
  Profile = -> Sketch018
  ReferenceAxis = -> Sketch018 [N_Axis]
  Refine = true
  Suppressed = false
  Type = 1
FEATURE [Sketcher::SketchObject] Sketch019
  ArcFitTolerance = 1e-06
  AttachmentSupport = -> [Pocket]
  ExternalGeometry = -> [Pocket]
  FullyConstrained = true
  MakeInternals = false
  MapMode = 5
  Placement = pos=(0,0,27.7) rot=(0,0,1;0rad)
  sketch-geometry (10):
    g0: ArcOfCircle CenterX=41.4 CenterY=34 CenterZ=0 NormalX=0 NormalY=0 NormalZ=1 AngleXU=0 Radius=9 StartAngle=4.71239 EndAngle=6.28319
    g1: ArcOfCircle CenterX=41.4 CenterY=-34 CenterZ=0 NormalX=0 NormalY=0 NormalZ=1 AngleXU=0 Radius=9 StartAngle=0 EndAngle=1.5708
    g2: LineSegment StartX=41.4 StartY=-34 StartZ=0 EndX=41.4 EndY=-25 EndZ=0
    g3: LineSegment StartX=41.4 StartY=-34 StartZ=0 EndX=50.4 EndY=-34 EndZ=0
    g4: LineSegment StartX=41.4 StartY=34 StartZ=0 EndX=41.4 EndY=25 EndZ=0
    g5: LineSegment StartX=41.4 StartY=34 StartZ=0 EndX=50.4 EndY=34 EndZ=0
    g6: LineSegment StartX=41.4 StartY=-10.5 StartZ=0 EndX=41.4 EndY=10.5 EndZ=0
    g7: ArcOfCircle CenterX=41.4 CenterY=1.5 CenterZ=0 NormalX=0 NormalY=0 NormalZ=1 AngleXU=0 Radius=9 StartAngle=-9.95e-14 EndAngle=1.5708
    g8: LineSegment StartX=50.4 StartY=1.5 StartZ=0 EndX=50.4 EndY=-1.49998 EndZ=0
    g9: ArcOfCircle CenterX=41.4 CenterY=-1.5 CenterZ=0 NormalX=0 NormalY=0 NormalZ=1 AngleXU=0 Radius=9 StartAngle=4.71239 EndAngle=6.28319
  constraints (26):
    c: Coincident(g0,g-4)
    c: Coincident(g0,g-4)
    c: PointOnObject(g0,g-3)
    c: Coincident(g1,g-5)
    c: Coincident(g1,g-5)
    c: PointOnObject(g1,g-3)
    c: Coincident(g2,g1)
    c: Coincident(g2,g1)
    c: Coincident(g3,g1)
    c: Coincident(g3,g1)
    c: Coincident(g4,g0)
    c: Coincident(g4,g0)
    c: Coincident(g5,g0)
    c: Coincident(g5,g0)
    c: PointOnObject(g6,g-3)
    c: Symmetric(g6,g6,g-1)
    c: Distance(g6) = 21
    c: PointOnObject(g7,g6)
    c: Coincident(g7,g6)
    c: Equal(g7,g0)
    c: Vertical(g8)
    c: Tangent(g8,g7) = 1.5708
    c: PointOnObject(g9,g6)
    c: Coincident(g9,g6)
    c: Equal(g7,g9)
    c: Coincident(g9,g8)
FEATURE [PartDesign::Pocket] Pocket011  label="Screw Driver Access"
  BaseFeature = -> Pocket
  Direction = (0,0,-1)
  Length = 13
  Length2 = 5
  Profile = -> Sketch019
  ReferenceAxis = -> Sketch019 [N_Axis]
  Refine = true
  Suppressed = false
  Type = 0
FEATURE [Sketcher::SketchObject] Sketch020
  ArcFitTolerance = 1e-06
  AttachmentSupport = -> [Pocket011]
  ExternalGeometry = -> [Pocket011]
  FullyConstrained = true
  MakeInternals = false
  MapMode = 5
  Placement = pos=(0,0,27.7) rot=(0,0,1;0rad)
  expr: Constraints[4] = VarSet.BlackSelfTappingDiameter
  sketch-geometry (7):
    g0: Circle CenterX=46.7 CenterY=18 CenterZ=0 NormalX=0 NormalY=0 NormalZ=1 AngleXU=0 Radius=1.35
    g1: Circle CenterX=46.7 CenterY=-18 CenterZ=0 NormalX=0 NormalY=0 NormalZ=1 AngleXU=0 Radius=1.35
    g2: LineSegment [constr] StartX=46.7 StartY=18 StartZ=0 EndX=46.7 EndY=-18 EndZ=0
    g3: LineSegment [constr] StartX=46.7 StartY=18 StartZ=0 EndX=41.4 EndY=18 EndZ=0
    g4: LineSegment [constr] StartX=46.7 StartY=18 StartZ=0 EndX=52 EndY=18 EndZ=0
    g5: LineSegment [constr] StartX=46.7 StartY=18 StartZ=0 EndX=52 EndY=34 EndZ=0
    g6: LineSegment [constr] StartX=52 StartY=-34 StartZ=0 EndX=46.7 EndY=-18 EndZ=0
  constraints (18):
    c: Coincident(g2,g0)
    c: Vertical(g2)
    c: Coincident(g2,g1)
    c: Equal(g1,g0)
    c: Diameter(g1) = 2.7
    c: Coincident(g3,g0)
    c: Horizontal(g3)
    c: Coincident(g4,g0)
    c: PointOnObject(g4,g-3)
    c: Horizontal(g4)
    c: Equal(g4,g3)
    c: Distance(g2) = 36
    c: PointOnObject(g3,g-4)
    c: Coincident(g5,g0)
    c: Coincident(g5,g-3)
    c: Coincident(g6,g-3)
    c: Coincident(g6,g1)
    c: Equal(g5,g6)
FEATURE [PartDesign::Pocket] Pocket012  label="Floor Screws"
  BaseFeature = -> Pocket011
  Direction = (0,0,-1)
  Length = 5
  Length2 = 5
  Profile = -> Sketch020
  ReferenceAxis = -> Sketch020 [N_Axis]
  Refine = true
  Suppressed = false
  Type = 0
FEATURE [Sketcher::SketchObject] Sketch021
  ArcFitTolerance = 1e-06
  AttachmentSupport = -> [Pocket012]
  ExternalGeometry = -> [Pocket012]
  FullyConstrained = true
  MakeInternals = false
  MapMode = 5
  Placement = pos=(0,34,0) rot=(0,0.707107,0.707107;3.14159rad)
  sketch-geometry (3):
    g0: LineSegment StartX=-50.4 StartY=10.7 StartZ=0 EndX=-43.4 EndY=10.7 EndZ=0
    g1: LineSegment StartX=-50.4 StartY=10.7 StartZ=0 EndX=-50.4 EndY=17.7 EndZ=0
    g2: LineSegment StartX=-43.4 StartY=10.7 StartZ=0 EndX=-50.4 EndY=17.7 EndZ=0
  constraints (8):
    c: Coincident(g0,g-3)
    c: Horizontal(g0)
    c: Coincident(g1,g0)
    c: Vertical(g1)
    c: Coincident(g2,g0)
    c: Coincident(g2,g1)
    c: Equal(g0,g1)
    c: Distance(g0) = 7
FEATURE [PartDesign::Pad] Pad007  label="Wall to Body 1"
  BaseFeature = -> Pocket012
  Direction = (0,1,-2e-16)
  Length = 1.6
  Length2 = 10
  Profile = -> Sketch021
  ReferenceAxis = -> Sketch021 [N_Axis]
  Refine = true
  Reversed = true
  Suppressed = false
  Type = 0
  expr: Length = VarSet.WallThickness
FEATURE [Sketcher::SketchObject] Sketch022
  ArcFitTolerance = 1e-06
  AttachmentSupport = -> [Pad007]
  ExternalGeometry = -> [Pad007]
  FullyConstrained = true
  MakeInternals = false
  MapMode = 5
  Placement = pos=(-6.764e-13,-34,-3.288e-13) rot=(1,0,0;1.5708rad)
  sketch-geometry (3):
    g0: LineSegment StartX=50.4 StartY=10.7 StartZ=0 EndX=43.4 EndY=10.7 EndZ=0
    g1: LineSegment StartX=50.4 StartY=10.7 StartZ=0 EndX=50.4 EndY=17.7 EndZ=0
    g2: LineSegment StartX=43.4 StartY=10.7 StartZ=0 EndX=50.4 EndY=17.7 EndZ=0
  constraints (8):
    c: Coincident(g0,g-3)
    c: Horizontal(g0)
    c: Coincident(g1,g0)
    c: Vertical(g1)
    c: Coincident(g2,g0)
    c: Coincident(g2,g1)
    c: Equal(g0,g1)
    c: Distance(g0) = 7
FEATURE [PartDesign::Pad] Pad008  label="Wall to Body 2"
  BaseFeature = -> Pad007
  Direction = (-1.99e-14,-1,-9.5e-15)
  Length = 1.6
  Length2 = 10
  Profile = -> Sketch022
  ReferenceAxis = -> Sketch022 [N_Axis]
  Refine = true
  Reversed = true
  Suppressed = false
  Type = 0
  expr: Length = VarSet.WallThickness
FEATURE [Sketcher::SketchObject] Sketch023
  ArcFitTolerance = 1e-06
  AttachmentSupport = -> [Pad008]
  ExternalGeometry = -> [Pad008]
  FullyConstrained = true
  MakeInternals = false
  MapMode = 5
  Placement = pos=(52,1.0692e-12,-4.0489e-12) rot=(0.57735,0.57735,0.57735;2.0944rad)
  sketch-geometry (4):
    g0: LineSegment StartX=-8 StartY=27.7 StartZ=0 EndX=8 EndY=27.7 EndZ=0
    g1: LineSegment StartX=4 StartY=23.7 StartZ=0 EndX=-3.99997 EndY=23.7 EndZ=0
    g2: ArcOfCircle CenterX=4 CenterY=27.7 CenterZ=0 NormalX=0 NormalY=0 NormalZ=1 AngleXU=0 Radius=4 StartAngle=4.71239 EndAngle=6.28319
    g3: ArcOfCircle CenterX=-4 CenterY=27.7 CenterZ=0 NormalX=0 NormalY=0 NormalZ=1 AngleXU=0 Radius=4 StartAngle=3.14159 EndAngle=4.7124
  constraints (12):
    c: PointOnObject(g0,g-3)
    c: Symmetric(g0,g0,g-2)
    c: Distance(g0) = 16
    c: Horizontal(g1)
    c: PointOnObject(g2,g0)
    c: Coincident(g2,g0)
    c: Diameter(g2) = 8
    c: Tangent(g2,g1) = 1.5708
    c: PointOnObject(g3,g0)
    c: Coincident(g3,g0)
    c: Equal(g3,g2)
    c: Coincident(g3,g1)
FEATURE [PartDesign::Pocket] Pocket013  label="RS232 Passage"
  BaseFeature = -> Pad008
  Direction = (-1,-2.04e-14,7.77e-14)
  Length = 5
  Length2 = 5
  Profile = -> Sketch023
  ReferenceAxis = -> Sketch023 [N_Axis]
  Refine = true
  Suppressed = false
  Type = 0
FEATURE [PartDesign::Body] Body
  AllowCompound = false
  Group = -> [Sketch,Pad,Sketch002,Pad001,Sketch003,Pad002,Pad004,Sketch004,Pad003,Sketch005,Pocket001,Sketch006,Pocket002,Sketch007,Pocket003,Sketch008,Pocket004,Sketch009,Pocket005,Sketch010,Pocket006,Sketch012,Pocket008,Sketch013,Pocket009,Sketch014,Pocket010,Sketch015,Sketch016,Pad005,Sketch017,Pad006,Sketch018,Pocket,Sketch019,Pocket011,Sketch020,Pocket012,Sketch021,Pad007,Sketch022,Pad008,Sketch023,+1 more]
  Origin = -> Origin
  Tip = -> Pocket013
